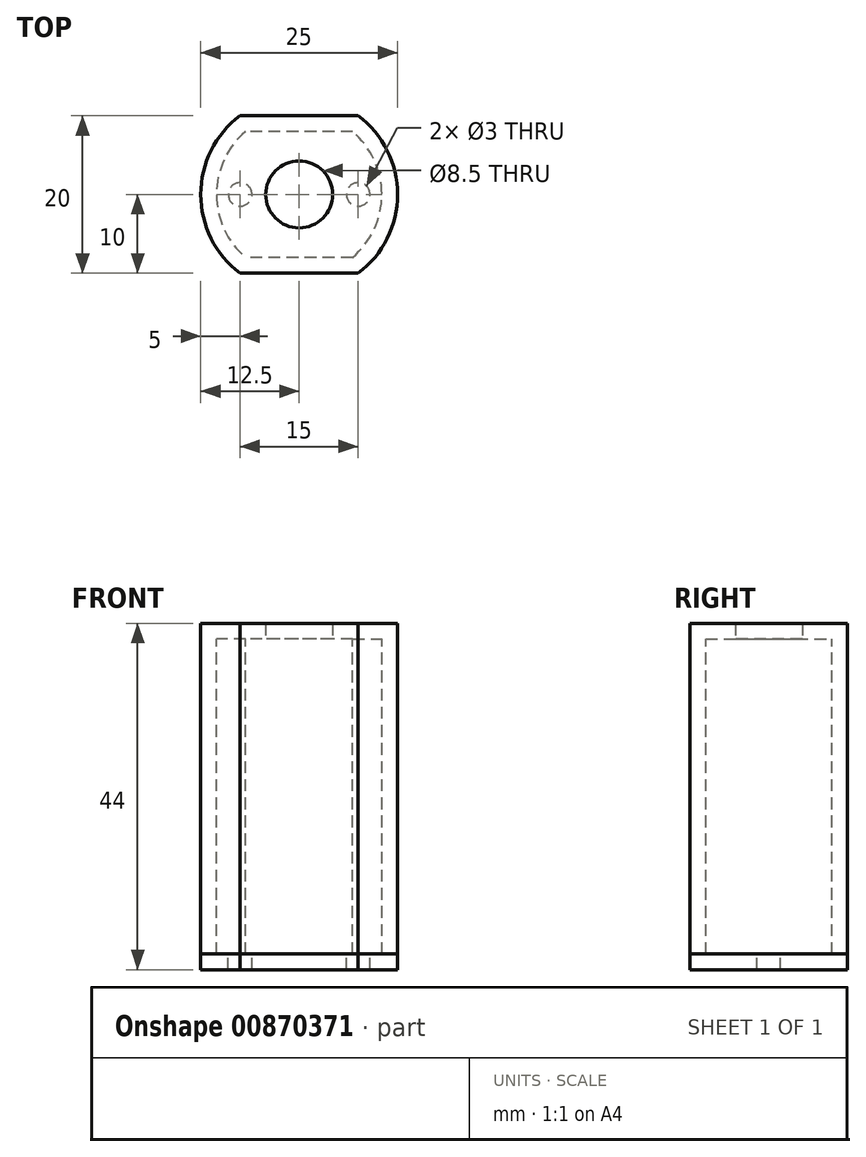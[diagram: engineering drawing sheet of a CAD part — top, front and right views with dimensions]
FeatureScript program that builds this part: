
annotation { "Feature Type Name" : "Feature", "Feature Type Description" : "" }
export const myFeature = defineFeature(function(context is Context, id is Id, definition is map)
    precondition{}
    {
        {
            var Q0;
            Q0=qCreatedBy(makeId("Top.planeOp"),FACE);
            var sketch = newSketch(context, id + "F0", { "sketchPlane" : qUnion([Q0])});
            skCircle(sketch, "E0", {"center": v(0, 0) * mm, "radius": 4.25 * mm});
            skArc(sketch, "E1", {"start": v(-6.8, 8) * mm, "mid": v(-10.5, 0) * mm, "end": v(-6.8, -8) * mm});
            skLineSegment(sketch, "E2", {"start": v(0, 0) * mm, "end": v(0, 8) * mm});
            skLineSegment(sketch, "E3", {"start": v(0, 8) * mm, "end": v(6.8, 8) * mm});
            skLineSegment(sketch, "E4", {"start": v(6.8, 8) * mm, "end": v(-6.8, 8) * mm});
            skLineSegment(sketch, "E5.MirrorCS", {"start": v(6.8, -8) * mm, "end": v(-6.8, -8) * mm});
            skArc(sketch, "E6.trimOffspring", {"start": v(6.8, -8) * mm, "mid": v(10.5, 0) * mm, "end": v(6.8, 8) * mm});
            skLineSegment(sketch, "E7.0", {"start": v(7.5, 10) * mm, "end": v(-7.5, 10) * mm});
            skArc(sketch, "E7.1", {"start": v(7.5, -10) * mm, "mid": v(12.5, 0) * mm, "end": v(7.5, 10) * mm});
            skLineSegment(sketch, "E7.2", {"start": v(7.5, -10) * mm, "end": v(-7.5, -10) * mm});
            skArc(sketch, "E7.3", {"start": v(-7.5, 10) * mm, "mid": v(-12.5, 0) * mm, "end": v(-7.5, -10) * mm});
            skSolve(sketch);
        }
        {
            var Q0;
            Q0=makeQuery(id+"F0.imprint","IMPRINT",FACE,{"disambiguationData":[TD([[makeQuery(id+"F0.imprint","IMPRINT",EDGE,{"derivedFrom":sQuery(id+"F0.wireOp",EDGE,"E0")}),-1.0]])]});
            var Q1;
            {var subQ1=sQuery(id+"F0.wireOp",EDGE,"E1");Q1=makeQuery(id+"F0.imprint","IMPRINT",FACE,{"disambiguationData":[TD([[makeQuery(id+"F0.imprint","IMPRINT",EDGE,{"derivedFrom":subQ1}),-1.0]])]});}
            extrude(context, id + "F1", {"entities" : qUnion([Q0, Q1]), "depth" : 2 * mm, "offsetDistance" : 25 * mm});
        }
        {
            var Q0;
            {var subQ1=sQuery(id+"F0.wireOp",EDGE,"E1");Q0=makeQuery(id+"F0.imprint","IMPRINT",FACE,{"disambiguationData":[TD([[makeQuery(id+"F0.imprint","IMPRINT",EDGE,{"derivedFrom":subQ1}),-1.0]])]});}
            extrude(context, id + "F2", {"entities" : qUnion([Q0]), "operationType" : NewBodyOperationType.ADD, "oppositeDirection" : true, "depth" : 40 * mm, "offsetDistance" : 25 * mm});
        }
        {
            var Q0;
            Q0=makeQuery(id+"F2.opExtrude","CAP_FACE",FACE,{"disambiguationData":[OSD([sQuery(id+"F0.wireOp",EDGE,"E1"),sQuery(id+"F0.wireOp",EDGE,"E4"),sQuery(id+"F0.wireOp",EDGE,"E5.MirrorCS"),sQuery(id+"F0.wireOp",EDGE,"E6.trimOffspring"),sQuery(id+"F0.wireOp",EDGE,"E7.0"),sQuery(id+"F0.wireOp",EDGE,"E7.1"),sQuery(id+"F0.wireOp",EDGE,"E7.2"),sQuery(id+"F0.wireOp",EDGE,"E7.3")])],"isStart":false});
            var sketch = newSketch(context, id + "F3", { "sketchPlane" : qUnion([Q0])});
            skCircle(sketch, "E8", {"center": v(7.5, 0) * mm, "radius": 1.5 * mm});
            skCircle(sketch, "E9", {"center": v(-7.5, 0) * mm, "radius": 1.5 * mm});
            skSolve(sketch);
        }
        {
            var Q0;
            Q0=makeQuery(id+"F3.imprint","IMPRINT",FACE,{"disambiguationData":[TD([[makeQuery(id+"F3.imprint","IMPRINT",EDGE,{"derivedFrom":makeQuery(id+"F2.opExtrude","CAP_EDGE",EDGE,{"disambiguationData":[OSD([sQuery(id+"F0.wireOp",EDGE,"E1")])],"isStart":false})}),1.0]])]});
            var Q1;
            Q1=makeQuery(id+"F3.imprint","IMPRINT",FACE,{"disambiguationData":[TD([[makeQuery(id+"F3.imprint","IMPRINT",EDGE,{"derivedFrom":sQuery(id+"F3.wireOp",EDGE,"E8")}),-1.0]])]});
            extrude(context, id + "F4", {"entities" : qUnion([Q0, Q1]), "depth" : 2 * mm, "offsetDistance" : 25 * mm});
        }
    });
